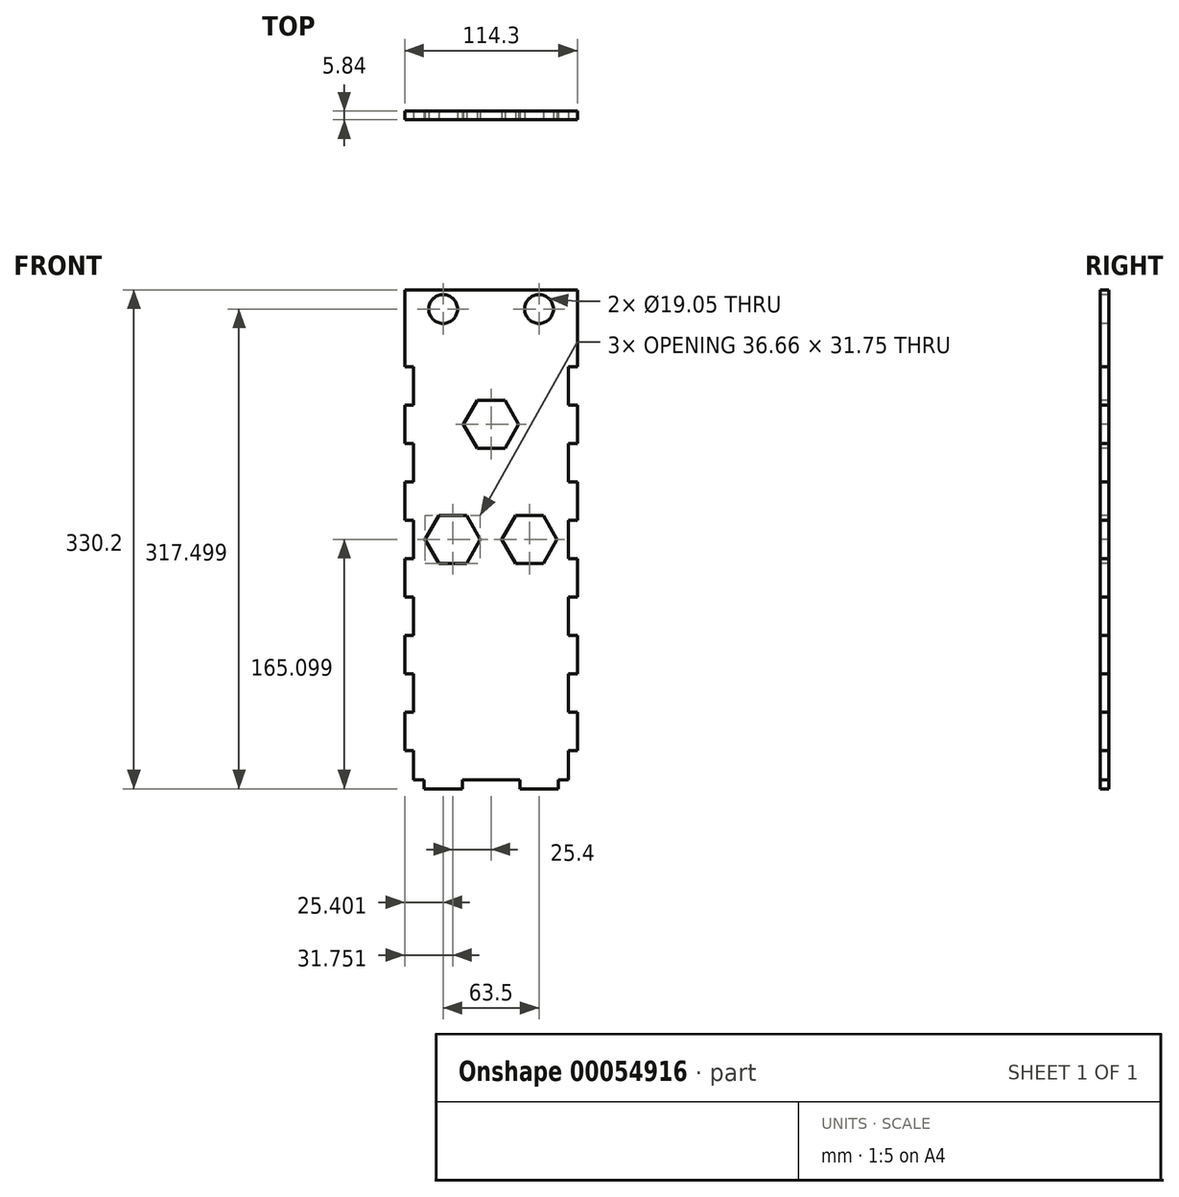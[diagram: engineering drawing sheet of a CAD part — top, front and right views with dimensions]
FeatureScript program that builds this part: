
annotation { "Feature Type Name" : "Feature", "Feature Type Description" : "" }
export const myFeature = defineFeature(function(context is Context, id is Id, definition is map)
    precondition{}
    {
        {
            var Q0;
            Q0=qCreatedBy(makeId("Front.planeOp"),FACE);
            var sketch = newSketch(context, id + "F0", { "sketchPlane" : qUnion([Q0])});
            skLineSegment(sketch, "E0.bottom", {"start": v(-82.6, 256.44) * mm, "end": v(31.7, 256.44) * mm});
            skLineSegment(sketch, "E0.top", {"start": v(-82.6, -73.76) * mm, "end": v(31.7, -73.76) * mm});
            skLineSegment(sketch, "E0.left", {"start": v(-82.6, 256.44) * mm, "end": v(-82.6, -73.76) * mm});
            skLineSegment(sketch, "E0.right", {"start": v(31.7, 256.44) * mm, "end": v(31.7, -73.76) * mm});
            skSolve(sketch);
        }
        {
            var Q0;
            Q0=makeQuery(id+"F0.imprint","IMPRINT",FACE,{"disambiguationData":[TD([[makeQuery(id+"F0.imprint","IMPRINT",EDGE,{"derivedFrom":sQuery(id+"F0.wireOp",EDGE,"E0.bottom")}),-1.0]])]});
            extrude(context, id + "F1", {"entities" : qUnion([Q0]), "depth" : 5.84 * mm});
        }
        {
            var Q0;
            Q0=makeQuery(id+"F1.opExtrude","CAP_FACE",FACE,{"disambiguationData":[OSD([sQuery(id+"F0.wireOp",EDGE,"E0.bottom"),sQuery(id+"F0.wireOp",EDGE,"E0.top"),sQuery(id+"F0.wireOp",EDGE,"E0.left"),sQuery(id+"F0.wireOp",EDGE,"E0.right")])],"isStart":false});
            var sketch = newSketch(context, id + "F2", { "sketchPlane" : qUnion([Q0])});
            skLineSegment(sketch, "E1.bottom", {"start": v(-69.9, -73.76) * mm, "end": v(-44.5, -73.76) * mm});
            skLineSegment(sketch, "E1.top", {"start": v(-69.9, -67.92) * mm, "end": v(-44.5, -67.92) * mm});
            skLineSegment(sketch, "E1.left", {"start": v(-69.9, -73.76) * mm, "end": v(-69.9, -67.92) * mm});
            skLineSegment(sketch, "E1.right", {"start": v(-44.5, -73.76) * mm, "end": v(-44.5, -67.92) * mm});
            skLineSegment(sketch, "E2.bottom", {"start": v(-6.4, -73.76) * mm, "end": v(19, -73.76) * mm});
            skLineSegment(sketch, "E2.top", {"start": v(-6.4, -67.92) * mm, "end": v(19, -67.92) * mm});
            skLineSegment(sketch, "E2.left", {"start": v(-6.4, -73.76) * mm, "end": v(-6.4, -67.92) * mm});
            skLineSegment(sketch, "E2.right", {"start": v(19, -73.76) * mm, "end": v(19, -67.92) * mm});
            skLineSegment(sketch, "E3.bottom", {"start": v(-82.6, -48.36) * mm, "end": v(-76.76, -48.36) * mm});
            skLineSegment(sketch, "E3.top", {"start": v(-82.6, -22.96) * mm, "end": v(-76.76, -22.96) * mm});
            skLineSegment(sketch, "E3.left", {"start": v(-82.6, -48.36) * mm, "end": v(-82.6, -22.96) * mm});
            skLineSegment(sketch, "E3.right", {"start": v(-76.76, -48.36) * mm, "end": v(-76.76, -22.96) * mm});
            skLineSegment(sketch, "E4.bottom", {"start": v(-82.6, 2.44) * mm, "end": v(-76.76, 2.44) * mm});
            skLineSegment(sketch, "E4.top", {"start": v(-82.6, 27.84) * mm, "end": v(-76.76, 27.84) * mm});
            skLineSegment(sketch, "E4.left", {"start": v(-82.6, 2.44) * mm, "end": v(-82.6, 27.84) * mm});
            skLineSegment(sketch, "E4.right", {"start": v(-76.76, 2.44) * mm, "end": v(-76.76, 27.84) * mm});
            skLineSegment(sketch, "E5.bottom", {"start": v(-82.6, 78.64) * mm, "end": v(-76.76, 78.64) * mm});
            skLineSegment(sketch, "E5.top", {"start": v(-82.6, 53.24) * mm, "end": v(-76.76, 53.24) * mm});
            skLineSegment(sketch, "E5.left", {"start": v(-82.6, 53.24) * mm, "end": v(-82.6, 78.64) * mm});
            skLineSegment(sketch, "E5.right", {"start": v(-76.76, 53.24) * mm, "end": v(-76.76, 78.64) * mm});
            skLineSegment(sketch, "E6.bottom", {"start": v(-82.6, 129.44) * mm, "end": v(-76.76, 129.44) * mm});
            skLineSegment(sketch, "E6.top", {"start": v(-82.6, 104.04) * mm, "end": v(-76.76, 104.04) * mm});
            skLineSegment(sketch, "E6.left", {"start": v(-82.6, 104.04) * mm, "end": v(-82.6, 129.44) * mm});
            skLineSegment(sketch, "E6.right", {"start": v(-76.76, 104.04) * mm, "end": v(-76.76, 129.44) * mm});
            skLineSegment(sketch, "E7.bottom", {"start": v(-82.6, 154.84) * mm, "end": v(-76.76, 154.84) * mm});
            skLineSegment(sketch, "E7.top", {"start": v(-82.6, 180.24) * mm, "end": v(-76.76, 180.24) * mm});
            skLineSegment(sketch, "E7.left", {"start": v(-82.6, 154.84) * mm, "end": v(-82.6, 180.24) * mm});
            skLineSegment(sketch, "E7.right", {"start": v(-76.76, 154.84) * mm, "end": v(-76.76, 180.24) * mm});
            skLineSegment(sketch, "E8.bottom", {"start": v(31.7, -48.36) * mm, "end": v(25.86, -48.36) * mm});
            skLineSegment(sketch, "E8.top", {"start": v(31.7, -22.96) * mm, "end": v(25.86, -22.96) * mm});
            skLineSegment(sketch, "E8.left", {"start": v(31.7, -48.36) * mm, "end": v(31.7, -22.96) * mm});
            skLineSegment(sketch, "E8.right", {"start": v(25.86, -48.36) * mm, "end": v(25.86, -22.96) * mm});
            skLineSegment(sketch, "E9.bottom", {"start": v(31.7, 2.44) * mm, "end": v(25.86, 2.44) * mm});
            skLineSegment(sketch, "E9.top", {"start": v(31.7, 27.84) * mm, "end": v(25.86, 27.84) * mm});
            skLineSegment(sketch, "E9.left", {"start": v(31.7, 2.44) * mm, "end": v(31.7, 27.84) * mm});
            skLineSegment(sketch, "E9.right", {"start": v(25.86, 2.44) * mm, "end": v(25.86, 27.84) * mm});
            skLineSegment(sketch, "E10.bottom", {"start": v(31.7, 53.24) * mm, "end": v(25.86, 53.24) * mm});
            skLineSegment(sketch, "E10.top", {"start": v(31.7, 78.64) * mm, "end": v(25.86, 78.64) * mm});
            skLineSegment(sketch, "E10.left", {"start": v(31.7, 53.24) * mm, "end": v(31.7, 78.64) * mm});
            skLineSegment(sketch, "E10.right", {"start": v(25.86, 53.24) * mm, "end": v(25.86, 78.64) * mm});
            skLineSegment(sketch, "E11.bottom", {"start": v(31.7, 104.04) * mm, "end": v(25.86, 104.04) * mm});
            skLineSegment(sketch, "E11.top", {"start": v(31.7, 129.44) * mm, "end": v(25.86, 129.44) * mm});
            skLineSegment(sketch, "E11.left", {"start": v(31.7, 104.04) * mm, "end": v(31.7, 129.44) * mm});
            skLineSegment(sketch, "E11.right", {"start": v(25.86, 104.04) * mm, "end": v(25.86, 129.44) * mm});
            skLineSegment(sketch, "E12.bottom", {"start": v(31.7, 154.84) * mm, "end": v(25.86, 154.84) * mm});
            skLineSegment(sketch, "E12.top", {"start": v(31.7, 180.24) * mm, "end": v(25.86, 180.24) * mm});
            skLineSegment(sketch, "E12.left", {"start": v(31.7, 154.84) * mm, "end": v(31.7, 180.24) * mm});
            skLineSegment(sketch, "E12.right", {"start": v(25.86, 154.84) * mm, "end": v(25.86, 180.24) * mm});
            skLineSegment(sketch, "E13.bottom", {"start": v(-82.6, 205.64) * mm, "end": v(-76.76, 205.64) * mm});
            skLineSegment(sketch, "E13.top", {"start": v(-82.6, 231.04) * mm, "end": v(-76.76, 231.04) * mm});
            skLineSegment(sketch, "E13.left", {"start": v(-82.6, 205.64) * mm, "end": v(-82.6, 231.04) * mm});
            skLineSegment(sketch, "E13.right", {"start": v(-76.76, 205.64) * mm, "end": v(-76.76, 231.04) * mm});
            skLineSegment(sketch, "E14.bottom", {"start": v(31.7, 205.64) * mm, "end": v(25.86, 205.64) * mm});
            skLineSegment(sketch, "E14.top", {"start": v(31.7, 231.04) * mm, "end": v(25.86, 231.04) * mm});
            skLineSegment(sketch, "E14.left", {"start": v(31.7, 205.64) * mm, "end": v(31.7, 231.04) * mm});
            skLineSegment(sketch, "E14.right", {"start": v(25.86, 205.64) * mm, "end": v(25.86, 231.04) * mm});
            skLineSegment(sketch, "E15", {"start": v(-76.76, -48.36) * mm, "end": v(-76.76, -67.92) * mm});
            skLineSegment(sketch, "E16", {"start": v(-69.9, -67.92) * mm, "end": v(-76.76, -67.92) * mm});
            skLineSegment(sketch, "E17", {"start": v(19, -67.92) * mm, "end": v(25.86, -67.92) * mm});
            skLineSegment(sketch, "E18", {"start": v(25.86, -48.36) * mm, "end": v(25.86, -67.92) * mm});
            skLineSegment(sketch, "E19", {"start": v(-44.5, -67.92) * mm, "end": v(-6.4, -67.92) * mm});
            skLineSegment(sketch, "E20", {"start": v(-76.76, -22.96) * mm, "end": v(-76.76, 2.44) * mm});
            skLineSegment(sketch, "E21", {"start": v(-76.76, 27.84) * mm, "end": v(-76.76, 53.24) * mm});
            skLineSegment(sketch, "E22", {"start": v(-76.76, 78.64) * mm, "end": v(-76.76, 104.04) * mm});
            skLineSegment(sketch, "E23", {"start": v(-76.76, 129.44) * mm, "end": v(-76.76, 154.84) * mm});
            skLineSegment(sketch, "E24", {"start": v(25.86, 154.84) * mm, "end": v(25.86, 129.44) * mm});
            skLineSegment(sketch, "E25", {"start": v(25.86, 104.04) * mm, "end": v(25.86, 78.64) * mm});
            skLineSegment(sketch, "E26", {"start": v(25.86, 53.24) * mm, "end": v(25.86, 27.84) * mm});
            skLineSegment(sketch, "E27", {"start": v(25.86, 2.44) * mm, "end": v(25.86, -22.96) * mm});
            skLineSegment(sketch, "E28", {"start": v(-76.76, 180.24) * mm, "end": v(-76.76, 205.64) * mm});
            skLineSegment(sketch, "E29", {"start": v(25.86, 180.24) * mm, "end": v(25.86, 205.64) * mm});
            skLineSegment(sketch, "E30.bottom", {"start": v(-76.76, 231.04) * mm, "end": v(-82.6, 231.04) * mm});
            skLineSegment(sketch, "E30.top", {"start": v(-76.76, 256.44) * mm, "end": v(-82.6, 256.44) * mm});
            skLineSegment(sketch, "E30.left", {"start": v(-76.76, 231.04) * mm, "end": v(-76.76, 256.44) * mm});
            skLineSegment(sketch, "E30.right", {"start": v(-82.6, 231.04) * mm, "end": v(-82.6, 256.44) * mm});
            skLineSegment(sketch, "E31.bottom", {"start": v(25.86, 231.04) * mm, "end": v(31.7, 231.04) * mm});
            skLineSegment(sketch, "E31.top", {"start": v(25.86, 256.44) * mm, "end": v(31.7, 256.44) * mm});
            skLineSegment(sketch, "E31.left", {"start": v(25.86, 231.04) * mm, "end": v(25.86, 256.44) * mm});
            skLineSegment(sketch, "E31.right", {"start": v(31.7, 231.04) * mm, "end": v(31.7, 256.44) * mm});
            skSolve(sketch);
        }
        {
            var Q0;
            {var subQ1=sQuery(id+"F2.wireOp",EDGE,"E1.left");Q0=makeQuery(id+"F2.imprint","IMPRINT",FACE,{"disambiguationData":[TD([[makeQuery(id+"F2.imprint","IMPRINT",EDGE,{"derivedFrom":subQ1}),1.0]])]});}
            var Q1;
            {var subQ0=sQuery(id+"F2.wireOp",EDGE,"E1.right");Q1=makeQuery(id+"F2.imprint","IMPRINT",FACE,{"disambiguationData":[TD([[makeQuery(id+"F2.imprint","IMPRINT",EDGE,{"derivedFrom":subQ0}),-1.0]])]});}
            var Q2;
            {var subQ4=sQuery(id+"F2.wireOp",EDGE,"E2.right");Q2=makeQuery(id+"F2.imprint","IMPRINT",FACE,{"disambiguationData":[TD([[makeQuery(id+"F2.imprint","IMPRINT",EDGE,{"derivedFrom":subQ4}),-1.0]])]});}
            var Q3;
            {var subQ0=sQuery(id+"F2.wireOp",EDGE,"E3.top");Q3=makeQuery(id+"F2.imprint","IMPRINT",FACE,{"disambiguationData":[TD([[makeQuery(id+"F2.imprint","IMPRINT",EDGE,{"derivedFrom":subQ0}),1.0]])]});}
            var Q4;
            {var subQ0=sQuery(id+"F2.wireOp",EDGE,"E8.top");Q4=makeQuery(id+"F2.imprint","IMPRINT",FACE,{"disambiguationData":[TD([[makeQuery(id+"F2.imprint","IMPRINT",EDGE,{"derivedFrom":subQ0}),-1.0]])]});}
            var Q5;
            {var subQ0=sQuery(id+"F2.wireOp",EDGE,"E4.top");Q5=makeQuery(id+"F2.imprint","IMPRINT",FACE,{"disambiguationData":[TD([[makeQuery(id+"F2.imprint","IMPRINT",EDGE,{"derivedFrom":subQ0}),1.0]])]});}
            var Q6;
            {var subQ0=sQuery(id+"F2.wireOp",EDGE,"E9.top");Q6=makeQuery(id+"F2.imprint","IMPRINT",FACE,{"disambiguationData":[TD([[makeQuery(id+"F2.imprint","IMPRINT",EDGE,{"derivedFrom":subQ0}),-1.0]])]});}
            var Q7;
            {var subQ0=sQuery(id+"F2.wireOp",EDGE,"E5.bottom");Q7=makeQuery(id+"F2.imprint","IMPRINT",FACE,{"disambiguationData":[TD([[makeQuery(id+"F2.imprint","IMPRINT",EDGE,{"derivedFrom":subQ0}),1.0]])]});}
            var Q8;
            {var subQ0=sQuery(id+"F2.wireOp",EDGE,"E10.top");Q8=makeQuery(id+"F2.imprint","IMPRINT",FACE,{"disambiguationData":[TD([[makeQuery(id+"F2.imprint","IMPRINT",EDGE,{"derivedFrom":subQ0}),-1.0]])]});}
            var Q9;
            {var subQ0=sQuery(id+"F2.wireOp",EDGE,"E6.bottom");Q9=makeQuery(id+"F2.imprint","IMPRINT",FACE,{"disambiguationData":[TD([[makeQuery(id+"F2.imprint","IMPRINT",EDGE,{"derivedFrom":subQ0}),1.0]])]});}
            var Q10;
            {var subQ0=sQuery(id+"F2.wireOp",EDGE,"E11.top");Q10=makeQuery(id+"F2.imprint","IMPRINT",FACE,{"disambiguationData":[TD([[makeQuery(id+"F2.imprint","IMPRINT",EDGE,{"derivedFrom":subQ0}),-1.0]])]});}
            var Q11;
            {var subQ0=sQuery(id+"F2.wireOp",EDGE,"E7.top");Q11=makeQuery(id+"F2.imprint","IMPRINT",FACE,{"disambiguationData":[TD([[makeQuery(id+"F2.imprint","IMPRINT",EDGE,{"derivedFrom":subQ0}),1.0]])]});}
            var Q12;
            {var subQ0=sQuery(id+"F2.wireOp",EDGE,"E12.top");Q12=makeQuery(id+"F2.imprint","IMPRINT",FACE,{"disambiguationData":[TD([[makeQuery(id+"F2.imprint","IMPRINT",EDGE,{"derivedFrom":subQ0}),-1.0]])]});}
            var Q13;
            Q13=makeQuery(id+"F2.imprint","IMPRINT",FACE,{"disambiguationData":[TD([[makeQuery(id+"F2.imprint","IMPRINT",EDGE,{"derivedFrom":sQuery(id+"F2.wireOp",EDGE,"E31.bottom")}),1.0]])]});
            var Q14;
            Q14=makeQuery(id+"F2.imprint","IMPRINT",FACE,{"disambiguationData":[TD([[makeQuery(id+"F2.imprint","IMPRINT",EDGE,{"derivedFrom":sQuery(id+"F2.wireOp",EDGE,"E30.bottom")}),-1.0]])]});
            extrude(context, id + "F3", {"entities" : qUnion([Q0, Q1, Q2, Q3, Q4, Q5, Q6, Q7, Q8, Q9, Q10, Q11, Q12, Q13, Q14]), "operationType" : NewBodyOperationType.REMOVE, "oppositeDirection" : true, "depth" : 25.4 * mm});
        }
        {
            var Q0;
            Q0=makeQuery(id+"F1.opExtrude","CAP_FACE",FACE,{"disambiguationData":[OSD([sQuery(id+"F0.wireOp",EDGE,"E0.bottom"),sQuery(id+"F0.wireOp",EDGE,"E0.top"),sQuery(id+"F0.wireOp",EDGE,"E0.left"),sQuery(id+"F0.wireOp",EDGE,"E0.right")])],"isStart":false});
            var sketch = newSketch(context, id + "F4", { "sketchPlane" : qUnion([Q0])});
            skCircle(sketch, "E32", {"center": v(-25.45, 167.54) * mm, "radius": 15.88 * mm});
            skPoint(sketch, "E33", {"position": v(-25.45, 256.44) * mm});
            skCircle(sketch, "E34", {"center": v(-57.2, 243.74) * mm, "radius": 9.53 * mm});
            skCircle(sketch, "E35", {"center": v(6.3, 243.74) * mm, "radius": 9.53 * mm});
            skLineSegment(sketch, "E36", {"start": v(6.3, 243.74) * mm, "end": v(-57.2, 243.74) * mm, "construction": true});
            skPoint(sketch, "E37", {"position": v(-25.45, 243.74) * mm});
            skLineSegment(sketch, "E38", {"start": v(-50.85, 91.34) * mm, "end": v(-0.05, 91.34) * mm, "construction": true});
            skCircle(sketch, "E39.cCircle", {"center": v(-50.85, 91.34) * mm, "radius": 15.88 * mm, "construction": true});
            skLineSegment(sketch, "E39.0", {"start": v(-41.68, 107.21) * mm, "end": v(-32.52, 91.34) * mm});
            skLineSegment(sketch, "E39.1", {"start": v(-32.52, 91.34) * mm, "end": v(-41.68, 75.46) * mm});
            skLineSegment(sketch, "E39.2", {"start": v(-41.68, 75.46) * mm, "end": v(-60.01, 75.46) * mm});
            skLineSegment(sketch, "E39.3", {"start": v(-60.01, 75.46) * mm, "end": v(-69.18, 91.34) * mm});
            skLineSegment(sketch, "E39.4", {"start": v(-69.18, 91.34) * mm, "end": v(-60.01, 107.21) * mm});
            skLineSegment(sketch, "E39.5", {"start": v(-60.01, 107.21) * mm, "end": v(-41.68, 107.21) * mm});
            skPoint(sketch, "E39.0.midPoint", {"position": v(-37.1, 99.28) * mm});
            skCircle(sketch, "E40.cCircle", {"center": v(-0.05, 91.34) * mm, "radius": 15.88 * mm, "construction": true});
            skLineSegment(sketch, "E40.0", {"start": v(9.12, 107.21) * mm, "end": v(18.28, 91.34) * mm});
            skLineSegment(sketch, "E40.1", {"start": v(18.28, 91.34) * mm, "end": v(9.12, 75.46) * mm});
            skLineSegment(sketch, "E40.2", {"start": v(9.12, 75.46) * mm, "end": v(-9.21, 75.46) * mm});
            skLineSegment(sketch, "E40.3", {"start": v(-9.21, 75.46) * mm, "end": v(-18.38, 91.34) * mm});
            skLineSegment(sketch, "E40.4", {"start": v(-18.38, 91.34) * mm, "end": v(-9.21, 107.21) * mm});
            skLineSegment(sketch, "E40.5", {"start": v(-9.21, 107.21) * mm, "end": v(9.12, 107.21) * mm});
            skPoint(sketch, "E40.0.midPoint", {"position": v(13.7, 99.28) * mm});
            skCircle(sketch, "E41.cCircle", {"center": v(-25.45, 167.54) * mm, "radius": 15.88 * mm, "construction": true});
            skLineSegment(sketch, "E41.0", {"start": v(-34.61, 183.41) * mm, "end": v(-16.28, 183.41) * mm});
            skLineSegment(sketch, "E41.1", {"start": v(-16.28, 183.41) * mm, "end": v(-7.12, 167.54) * mm});
            skLineSegment(sketch, "E41.2", {"start": v(-7.12, 167.54) * mm, "end": v(-16.28, 151.66) * mm});
            skLineSegment(sketch, "E41.3", {"start": v(-16.28, 151.66) * mm, "end": v(-34.61, 151.66) * mm});
            skLineSegment(sketch, "E41.4", {"start": v(-34.61, 151.66) * mm, "end": v(-43.78, 167.54) * mm});
            skLineSegment(sketch, "E41.5", {"start": v(-43.78, 167.54) * mm, "end": v(-34.61, 183.41) * mm});
            skPoint(sketch, "E41.0.midPoint", {"position": v(-25.45, 183.41) * mm});
            skSolve(sketch);
        }
        {
            var Q0;
            Q0=makeQuery(id+"F4.imprint","IMPRINT",FACE,{"disambiguationData":[TD([[makeQuery(id+"F4.imprint","IMPRINT",EDGE,{"derivedFrom":sQuery(id+"F4.wireOp",EDGE,"75051fe7-244c-4015-a3ea-d51cca576220")}),1.0]])]});
            var Q1;
            Q1=makeQuery(id+"F4.imprint","IMPRINT",FACE,{"disambiguationData":[TD([[makeQuery(id+"F4.imprint","IMPRINT",EDGE,{"derivedFrom":sQuery(id+"F4.wireOp",EDGE,"c2ee280f-5fdd-4814-bd3f-3a15314b10c9")}),1.0]])]});
            var Q2;
            Q2=makeQuery(id+"F4.imprint","IMPRINT",FACE,{"disambiguationData":[TD([[makeQuery(id+"F4.imprint","IMPRINT",EDGE,{"derivedFrom":sQuery(id+"F4.wireOp",EDGE,"E32")}),1.0]])]});
            var Q3;
            Q3=makeQuery(id+"F4.imprint","IMPRINT",FACE,{"disambiguationData":[TD([[makeQuery(id+"F4.imprint","IMPRINT",EDGE,{"derivedFrom":sQuery(id+"F4.wireOp",EDGE,"E34")}),1.0]])]});
            var Q4;
            Q4=makeQuery(id+"F4.imprint","IMPRINT",FACE,{"disambiguationData":[TD([[makeQuery(id+"F4.imprint","IMPRINT",EDGE,{"derivedFrom":sQuery(id+"F4.wireOp",EDGE,"E35")}),1.0]])]});
            var Q5;
            Q5=makeQuery(id+"F4.imprint","IMPRINT",FACE,{"disambiguationData":[TD([[makeQuery(id+"F4.imprint","IMPRINT",EDGE,{"derivedFrom":sQuery(id+"F4.wireOp",EDGE,"E39.0")}),-1.0]])]});
            var Q6;
            Q6=makeQuery(id+"F4.imprint","IMPRINT",FACE,{"disambiguationData":[TD([[makeQuery(id+"F4.imprint","IMPRINT",EDGE,{"derivedFrom":sQuery(id+"F4.wireOp",EDGE,"E40.0")}),-1.0]])]});
            var Q7;
            {var subQ0=sQuery(id+"F4.wireOp",EDGE,"E41.0");var subQ1=sQuery(id+"F4.wireOp",EDGE,"E32");var subQ2=makeQuery(id+"F4.imprint","INTERSECT",VERTEX,{"derivedFrom":[subQ1,subQ0]});Q7=makeQuery(id+"F4.imprint","IMPRINT",FACE,{"disambiguationData":[TD([[makeQuery(id+"F4.imprint","IMPRINT",EDGE,{"disambiguationData":[TD([[subQ2,-1.0]])],"derivedFrom":subQ1}),-1.0]])]});}
            var Q8;
            {var subQ0=sQuery(id+"F4.wireOp",EDGE,"E41.0");var subQ1=sQuery(id+"F4.wireOp",EDGE,"E32");var subQ2=makeQuery(id+"F4.imprint","INTERSECT",VERTEX,{"derivedFrom":[subQ1,subQ0]});Q8=makeQuery(id+"F4.imprint","IMPRINT",FACE,{"disambiguationData":[TD([[makeQuery(id+"F4.imprint","IMPRINT",EDGE,{"disambiguationData":[TD([[subQ2,1.0]])],"derivedFrom":subQ1}),-1.0]])]});}
            var Q9;
            {var subQ0=sQuery(id+"F4.wireOp",EDGE,"E41.1");var subQ1=sQuery(id+"F4.wireOp",EDGE,"E32");var subQ2=makeQuery(id+"F4.imprint","INTERSECT",VERTEX,{"derivedFrom":[subQ1,subQ0]});Q9=makeQuery(id+"F4.imprint","IMPRINT",FACE,{"disambiguationData":[TD([[makeQuery(id+"F4.imprint","IMPRINT",EDGE,{"disambiguationData":[TD([[subQ2,1.0]])],"derivedFrom":subQ1}),-1.0]])]});}
            var Q10;
            {var subQ0=sQuery(id+"F4.wireOp",EDGE,"E41.3");var subQ1=sQuery(id+"F4.wireOp",EDGE,"E32");var subQ2=makeQuery(id+"F4.imprint","INTERSECT",VERTEX,{"derivedFrom":[subQ1,subQ0]});Q10=makeQuery(id+"F4.imprint","IMPRINT",FACE,{"disambiguationData":[TD([[makeQuery(id+"F4.imprint","IMPRINT",EDGE,{"disambiguationData":[TD([[subQ2,-1.0]])],"derivedFrom":subQ1}),-1.0]])]});}
            var Q11;
            {var subQ0=sQuery(id+"F4.wireOp",EDGE,"E41.4");var subQ1=sQuery(id+"F4.wireOp",EDGE,"E32");var subQ2=makeQuery(id+"F4.imprint","INTERSECT",VERTEX,{"derivedFrom":[subQ1,subQ0]});Q11=makeQuery(id+"F4.imprint","IMPRINT",FACE,{"disambiguationData":[TD([[makeQuery(id+"F4.imprint","IMPRINT",EDGE,{"disambiguationData":[TD([[subQ2,-1.0]])],"derivedFrom":subQ1}),-1.0]])]});}
            var Q12;
            {var subQ0=sQuery(id+"F4.wireOp",EDGE,"E41.5");var subQ1=sQuery(id+"F4.wireOp",EDGE,"E32");var subQ2=makeQuery(id+"F4.imprint","INTERSECT",VERTEX,{"derivedFrom":[subQ1,subQ0]});Q12=makeQuery(id+"F4.imprint","IMPRINT",FACE,{"disambiguationData":[TD([[makeQuery(id+"F4.imprint","IMPRINT",EDGE,{"disambiguationData":[TD([[subQ2,-1.0]])],"derivedFrom":subQ1}),-1.0]])]});}
            var Q13;
            Q13=makeQuery(id+"F1.opExtrude","CAP_FACE",FACE,{"disambiguationData":[OSD([sQuery(id+"F0.wireOp",EDGE,"E0.bottom"),sQuery(id+"F0.wireOp",EDGE,"E0.top"),sQuery(id+"F0.wireOp",EDGE,"E0.left"),sQuery(id+"F0.wireOp",EDGE,"E0.right")])],"isStart":true});
            extrude(context, id + "F5", {"entities" : qUnion([Q0, Q1, Q2, Q3, Q4, Q5, Q6, Q7, Q8, Q9, Q10, Q11, Q12]), "operationType" : NewBodyOperationType.REMOVE, "endBound" : BoundingType.UP_TO_SURFACE, "oppositeDirection" : true, "endBoundEntityFace" : qUnion([Q13]), "depth" : 25.4 * mm});
        }
    });
